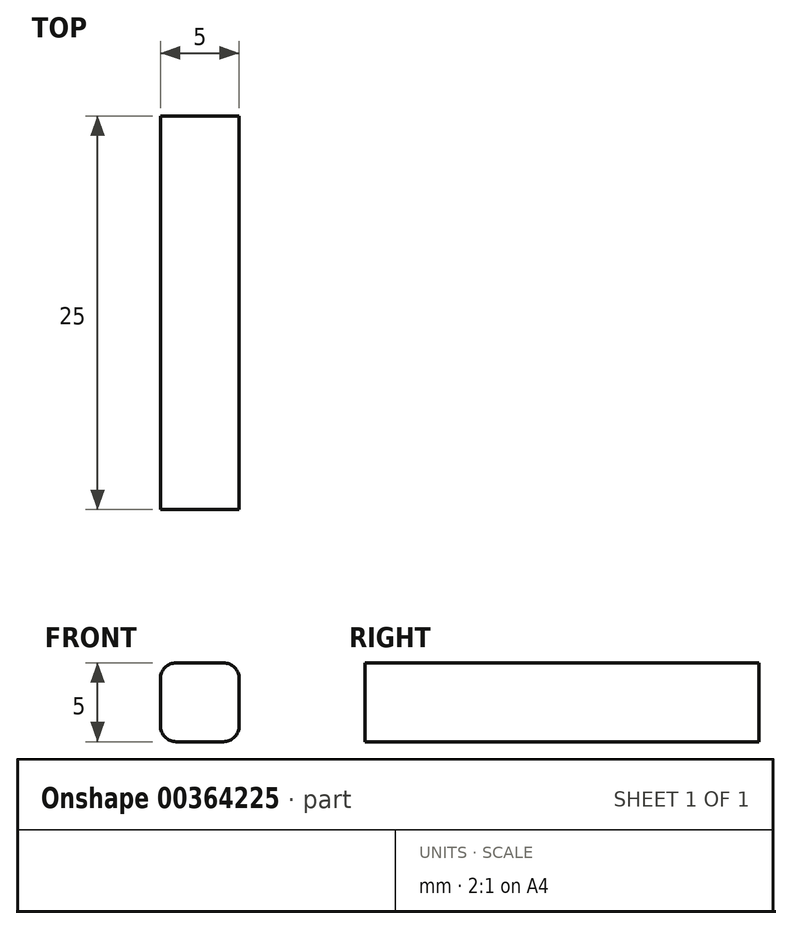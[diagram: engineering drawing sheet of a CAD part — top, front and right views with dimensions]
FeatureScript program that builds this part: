
annotation { "Feature Type Name" : "Feature", "Feature Type Description" : "" }
export const myFeature = defineFeature(function(context is Context, id is Id, definition is map)
    precondition{}
    {
        {
            var Q0;
            Q0=qCreatedBy(makeId("Front.planeOp"),FACE);
            var sketch = newSketch(context, id + "F0", { "sketchPlane" : qUnion([Q0])});
            skLineSegment(sketch, "E0.bottom", {"start": v(1.5, 2.5) * mm, "end": v(-1.5, 2.5) * mm});
            skLineSegment(sketch, "E0.top", {"start": v(1.5, -2.5) * mm, "end": v(-1.5, -2.5) * mm});
            skLineSegment(sketch, "E0.left", {"start": v(2.5, 1.5) * mm, "end": v(2.5, -1.5) * mm});
            skLineSegment(sketch, "E0.right", {"start": v(-2.5, 1.5) * mm, "end": v(-2.5, -1.5) * mm});
            skPoint(sketch, "E0.middle", {"position": v(0, 0) * mm});
            skPoint(sketch, "E1.visualSharp", {"position": v(-2.5, 2.5) * mm});
            skArc(sketch, "E1.filletArc", {"start": v(-1.5, 2.5) * mm, "mid": v(-2.2, 2.2) * mm, "end": v(-2.5, 1.5) * mm});
            skPoint(sketch, "E2.visualSharp", {"position": v(2.5, 2.5) * mm});
            skArc(sketch, "E2.filletArc", {"start": v(2.5, 1.5) * mm, "mid": v(2.2, 2.2) * mm, "end": v(1.5, 2.5) * mm});
            skPoint(sketch, "E3.visualSharp", {"position": v(2.5, -2.5) * mm});
            skArc(sketch, "E3.filletArc", {"start": v(1.5, -2.5) * mm, "mid": v(2.2, -2.2) * mm, "end": v(2.5, -1.5) * mm});
            skPoint(sketch, "E4.visualSharp", {"position": v(-2.5, -2.5) * mm});
            skArc(sketch, "E4.filletArc", {"start": v(-2.5, -1.5) * mm, "mid": v(-2.2, -2.2) * mm, "end": v(-1.5, -2.5) * mm});
            skSolve(sketch);
        }
        {
            var Q0;
            Q0=makeQuery(id+"F0.imprint","IMPRINT",FACE,{"disambiguationData":[TD([[makeQuery(id+"F0.imprint","IMPRINT",EDGE,{"derivedFrom":sQuery(id+"F0.wireOp",EDGE,"E0.bottom")}),1.0]])]});
            extrude(context, id + "F1", {"entities" : qUnion([Q0]), "depth" : 25 * mm});
        }
    });
